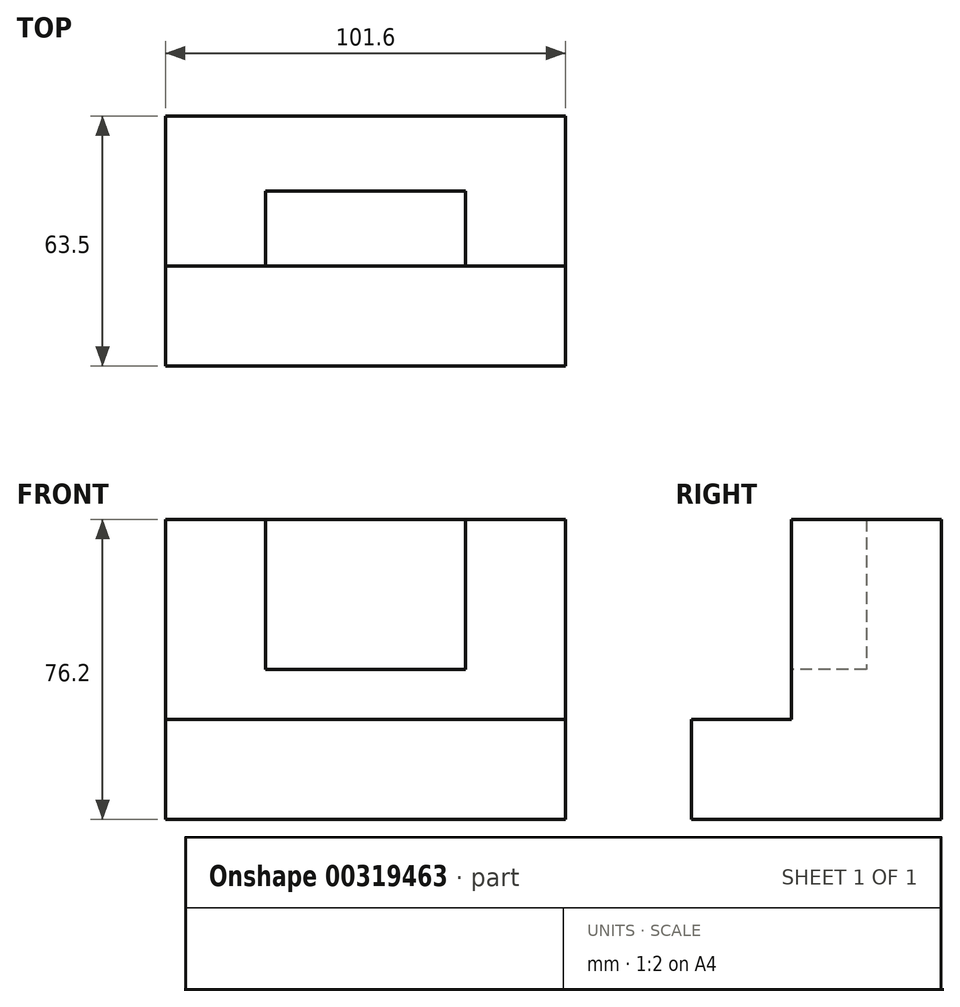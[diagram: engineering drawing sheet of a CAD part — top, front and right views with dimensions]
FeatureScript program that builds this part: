
annotation { "Feature Type Name" : "Feature", "Feature Type Description" : "" }
export const myFeature = defineFeature(function(context is Context, id is Id, definition is map)
    precondition{}
    {
        {
            var Q0;
            Q0=qCreatedBy(makeId("Right.planeOp"),FACE);
            var sketch = newSketch(context, id + "F0", { "sketchPlane" : qUnion([Q0])});
            skLineSegment(sketch, "E0", {"start": v(-25.7, -35.5) * mm, "end": v(37.8, -35.5) * mm});
            skLineSegment(sketch, "E1", {"start": v(37.8, -35.5) * mm, "end": v(37.8, 40.7) * mm});
            skLineSegment(sketch, "E2", {"start": v(37.8, 40.7) * mm, "end": v(-0.3, 40.7) * mm});
            skLineSegment(sketch, "E3", {"start": v(-0.3, 40.7) * mm, "end": v(-0.3, -10.1) * mm});
            skLineSegment(sketch, "E4", {"start": v(-0.3, -10.1) * mm, "end": v(-25.7, -10.1) * mm});
            skLineSegment(sketch, "E5", {"start": v(-25.7, -10.1) * mm, "end": v(-25.7, -35.5) * mm});
            skSolve(sketch);
        }
        {
            var Q0;
            Q0=makeQuery(id+"F0.imprint","IMPRINT",FACE,{"disambiguationData":[TD([[makeQuery(id+"F0.imprint","IMPRINT",EDGE,{"derivedFrom":sQuery(id+"F0.wireOp",EDGE,"E0")}),1.0]])]});
            extrude(context, id + "F1", {"entities" : qUnion([Q0]), "depth" : 101.6 * mm});
        }
        {
            var Q0;
            Q0=makeQuery(id+"F1.opExtrude","SWEPT_FACE",FACE,{"disambiguationData":[OSD([sQuery(id+"F0.wireOp",EDGE,"E3")])]});
            var sketch = newSketch(context, id + "F2", { "sketchPlane" : qUnion([Q0])});
            skLineSegment(sketch, "E6.bottom", {"start": v(25.4, 40.7) * mm, "end": v(76.2, 40.7) * mm});
            skLineSegment(sketch, "E6.top", {"start": v(25.4, 2.6) * mm, "end": v(76.2, 2.6) * mm});
            skLineSegment(sketch, "E6.left", {"start": v(25.4, 40.7) * mm, "end": v(25.4, 2.6) * mm});
            skLineSegment(sketch, "E6.right", {"start": v(76.2, 40.7) * mm, "end": v(76.2, 2.6) * mm});
            skSolve(sketch);
        }
        {
            var Q0;
            Q0=makeQuery(id+"F2.imprint","IMPRINT",FACE,{"disambiguationData":[TD([[makeQuery(id+"F2.imprint","IMPRINT",EDGE,{"derivedFrom":sQuery(id+"F2.wireOp",EDGE,"E6.bottom")}),1.0]])]});
            extrude(context, id + "F3", {"entities" : qUnion([Q0]), "operationType" : NewBodyOperationType.REMOVE, "oppositeDirection" : true, "depth" : 19.05 * mm});
        }
    });
